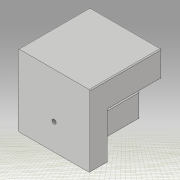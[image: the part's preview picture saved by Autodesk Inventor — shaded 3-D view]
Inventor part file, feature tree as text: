
AUTODESK INVENTOR PART (.ipt)
format: ipt  version: 2018 (Build 220112000, 112)  size: 322,048 bytes
history: native  units: in
note: dims shown in document units (in); Inventor stores cm internally (conversion verified against a paired STEP export)
features: extrude x10, sketch x9, projected_geometry x4, mirror x3, reference x3, other x2, plane x1, fillet x1
ambient origin geometry x8: Origin, YZ Plane, XZ Plane, XY Plane, X Axis, Y Axis, Z Axis, Center Point
bodies: Solid1 (feature_tree)
feature tree (33):
  extrude  "Extrusion1"  Depth=2.0in
  extrude  "Extrusion2"  Depth=0.911in
  extrude  "Extrusion3"  Depth=2.0in TaperAngle=0.0deg
  extrude  "Extrusion4"  Depth=2.0in TaperAngle=0.0deg
  plane  "Work Plane1"
  mirror  "Mirror1"
  extrude  "Extrusion5"  Depth=0.07in
  extrude  "Extrusion6"  Depth=1.0in TaperAngle=0.0deg
  mirror  "Mirror2"
  extrude  "Extrusion7"  Depth=0.5in
  mirror  "Mirror3"
  extrude  "Extrusion8"  Depth=0.025in TaperAngle=0.0deg
  fillet  "Fillet1"  Radius=0.025in
  extrude  "Extrusion9"  Depth=0.17in
  extrude  "Extrusion10"  Depth=0.43in
  sketch  "Sketch1"  dims[d0=2.0in d1=2.0in]
  sketch  "Sketch3"  dims[d2=2.0in d3=0.0in d4=0.911in]
  reference  "Reference1"
  reference  "Reference2"
  reference  "Reference3"
  sketch  "Sketch4"  dims[d5=0.681in d6=2.0in d7=0.0in]
  sketch  "Sketch5"  dims[d8=0.002in d9=2.0in d10=0.0in]
  sketch  "Sketch6"  dims[d11=0.06in d12=0.07in]
  projected_geometry  "Projected Loop2"
  sketch  "Sketch7"  dims[d13=1.0in d14=0.0in d15=1.0in d16=0.0in]
  sketch  "Sketch8"  dims[d17=1.0in d18=0.0in d19=0.5in]
  sketch  "Sketch9"  dims[d20=1.0in d21=0.0in d22=0.025in d23=0.0in d24=0.025in]
  projected_geometry  "Projected Loop3"
  projected_geometry  "Projected Loop4"
  sketch  "Sketch10"  dims[d25=0.085in d26=0.17in d27=0.43in d28=0.025in d29=0.0in d30=0.115in d31=1.5in d32=0.0in]
  projected_geometry  "Projected Loop5"
  other  "Assembly2"
  other  "Jig 4 retaining Block:1"
